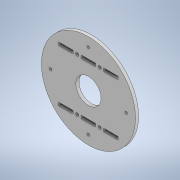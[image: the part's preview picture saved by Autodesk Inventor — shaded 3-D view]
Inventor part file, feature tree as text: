
AUTODESK INVENTOR PART (.ipt)
format: ipt  version: 2022 (Build 260153000, 153)  size: 178,688 bytes
history: native  units: mm
features: extrude x1, sketch x1
ambient origin geometry x8: Origin, YZ Plane, XZ Plane, XY Plane, X Axis, Y Axis, Z Axis, Center Point
bodies: Body1 (feature_tree)
feature tree (2):
  extrude  "Extrusion2"  Depth=22.0mm
  sketch  "Sketch3"  dims[d32=2.5mm d33=2.5mm d34=2.5mm d35=2.5mm d45=3.1mm d46=3.1mm d47=3.1mm d50=14.0mm d51=4.0mm d53=14.0mm d54=4.0mm d57=14.0mm d58=14.0mm d59=14.0mm d60=3.0mm d61=14.0mm d62=3.0mm d63=0.0mm d64=3.0mm d65=3.0mm d71=1.5mm d72=1.5mm d74=92.0mm d75=74.0mm d78=24.6mm d80=3.1mm d81=25.5mm d82=25.5mm d83=22.0mm d84=11.0mm d87=4.0mm d91=22.0mm d92=1.5mm d93=1.5mm d94=1.5mm d95=1.5mm d96=1.5mm d97=1.5mm d98=4.0mm]
